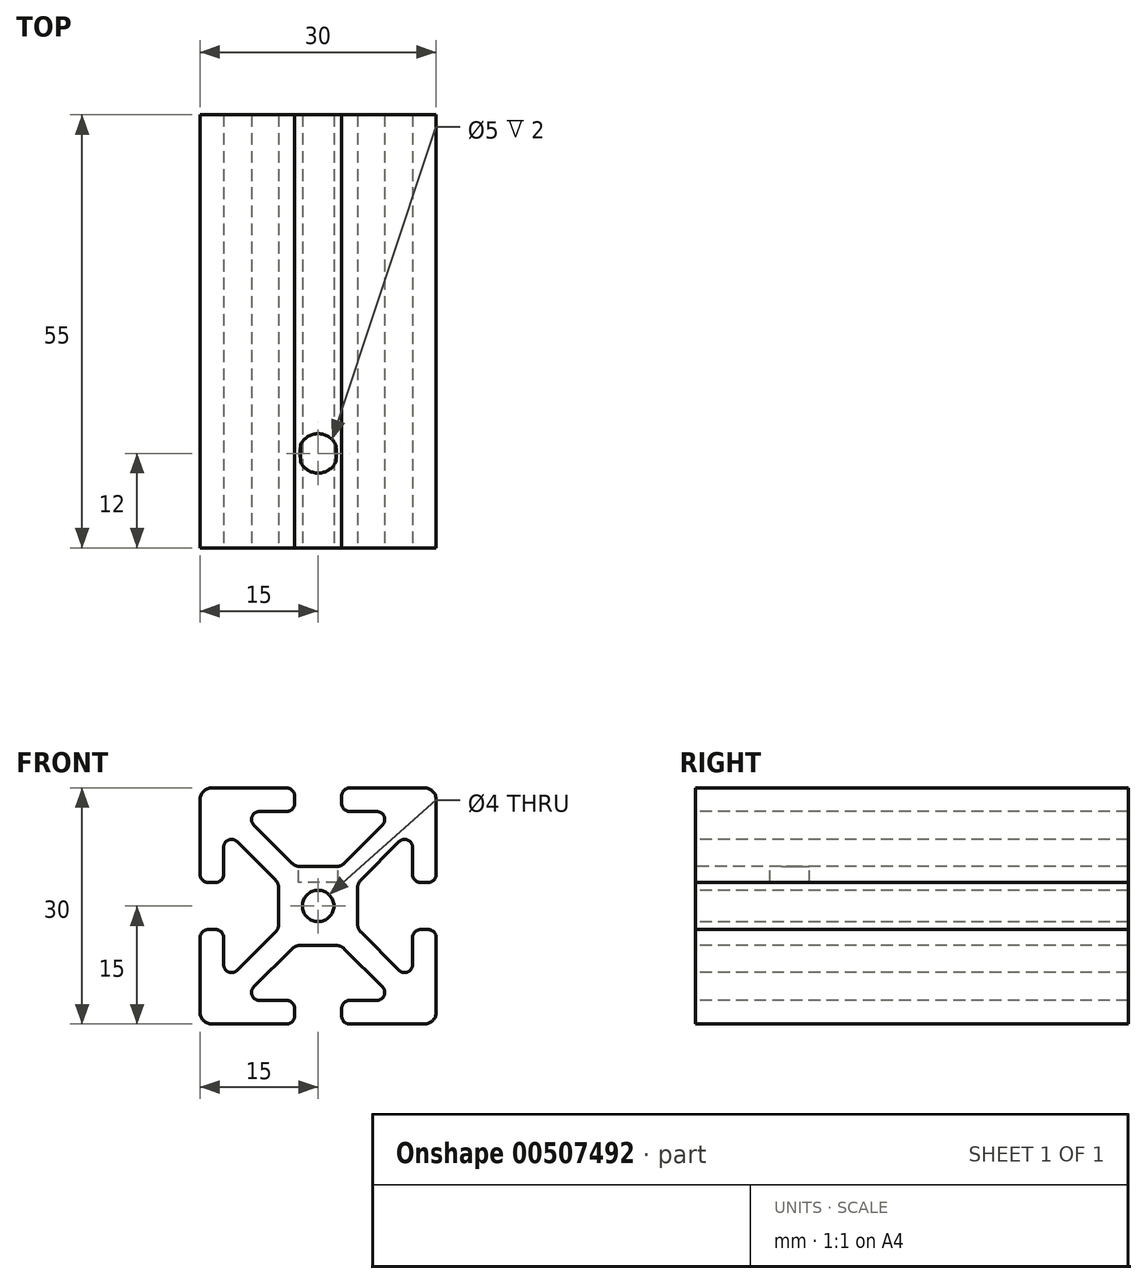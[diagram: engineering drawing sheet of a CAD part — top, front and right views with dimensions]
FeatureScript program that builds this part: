
annotation { "Feature Type Name" : "Feature", "Feature Type Description" : "" }
export const myFeature = defineFeature(function(context is Context, id is Id, definition is map)
    precondition{}
    {
        {
            var Q0;
            Q0=qCreatedBy(makeId("Front.planeOp"),FACE);
            var sketch = newSketch(context, id + "F0", { "sketchPlane" : qUnion([Q0])});
            skLineSegment(sketch, "E0.bottom", {"start": v(13.5, 15) * mm, "end": v(4, 15) * mm});
            skLineSegment(sketch, "E0.top", {"start": v(13.5, -15) * mm, "end": v(4, -15) * mm});
            skLineSegment(sketch, "E0.left", {"start": v(15, 13.5) * mm, "end": v(15, 4) * mm});
            skLineSegment(sketch, "E0.right", {"start": v(-15, 13.5) * mm, "end": v(-15, 4) * mm});
            skPoint(sketch, "E0.middle", {"position": v(0, 0) * mm});
            skLineSegment(sketch, "E1.bottom", {"start": v(7.46, 12) * mm, "end": v(4, 12) * mm});
            skLineSegment(sketch, "E1.top", {"start": v(7.46, -12) * mm, "end": v(4, -12) * mm});
            skLineSegment(sketch, "E1.left", {"start": v(12, 7.46) * mm, "end": v(12, 4) * mm});
            skLineSegment(sketch, "E1.right", {"start": v(-12, 7.46) * mm, "end": v(-12, 4) * mm});
            skLineSegment(sketch, "E2", {"start": v(8.17, 10.3) * mm, "end": v(3.32, 5.44) * mm});
            skLineSegment(sketch, "E3", {"start": v(-8.17, -10.3) * mm, "end": v(-3.32, -5.44) * mm});
            skLineSegment(sketch, "E4", {"start": v(-8.17, 10.3) * mm, "end": v(-3.32, 5.44) * mm});
            skLineSegment(sketch, "E5", {"start": v(-10.3, 8.17) * mm, "end": v(-5.44, 3.32) * mm});
            skPoint(sketch, "E6.orphan", {"position": v(12, 12) * mm});
            skPoint(sketch, "E7.orphan", {"position": v(12, -12) * mm});
            skPoint(sketch, "E8.orphan", {"position": v(-12, -12) * mm});
            skPoint(sketch, "E9.orphan", {"position": v(-12, 12) * mm});
            skLineSegment(sketch, "E10.trimOffspring", {"start": v(-5.44, -3.32) * mm, "end": v(-10.3, -8.17) * mm});
            skLineSegment(sketch, "E11.trimOffspring", {"start": v(5.44, -3.32) * mm, "end": v(10.3, -8.17) * mm});
            skLineSegment(sketch, "E12.trimOffspring", {"start": v(5.44, 3.32) * mm, "end": v(10.3, 8.17) * mm});
            skLineSegment(sketch, "E13.trimOffspring", {"start": v(3.32, -5.44) * mm, "end": v(8.17, -10.3) * mm});
            skLineSegment(sketch, "E14.bottom", {"start": v(2.26, 5) * mm, "end": v(-2.26, 5) * mm});
            skLineSegment(sketch, "E14.top", {"start": v(2.26, -5) * mm, "end": v(-2.26, -5) * mm});
            skLineSegment(sketch, "E14.left", {"start": v(5, 2.26) * mm, "end": v(5, -2.26) * mm});
            skLineSegment(sketch, "E14.right", {"start": v(-5, 2.26) * mm, "end": v(-5, -2.26) * mm});
            skPoint(sketch, "E15.orphan", {"position": v(5, 5) * mm});
            skPoint(sketch, "E16.orphan", {"position": v(5, -5) * mm});
            skPoint(sketch, "E17.orphan", {"position": v(-5, -5) * mm});
            skPoint(sketch, "E18.orphan", {"position": v(-5, 5) * mm});
            skCircle(sketch, "E19", {"center": v(0, 0) * mm, "radius": 2 * mm});
            skLineSegment(sketch, "E20", {"start": v(-3, 14) * mm, "end": v(-3, 13) * mm});
            skLineSegment(sketch, "E21", {"start": v(3, 14) * mm, "end": v(3, 13) * mm});
            skLineSegment(sketch, "E22.trimOffspring", {"start": v(-3, -13) * mm, "end": v(-3, -14) * mm});
            skLineSegment(sketch, "E23.trimOffspring", {"start": v(-4, 12) * mm, "end": v(-7.46, 12) * mm});
            skLineSegment(sketch, "E24.trimOffspring", {"start": v(-4, 15) * mm, "end": v(-13.5, 15) * mm});
            skLineSegment(sketch, "E25.trimOffspring", {"start": v(3, -13) * mm, "end": v(3, -14) * mm});
            skLineSegment(sketch, "E26.trimOffspring", {"start": v(-4, -12) * mm, "end": v(-7.46, -12) * mm});
            skLineSegment(sketch, "E27.trimOffspring", {"start": v(-4, -15) * mm, "end": v(-13.5, -15) * mm});
            skLineSegment(sketch, "E28", {"start": v(-14, 3) * mm, "end": v(-13, 3) * mm});
            skLineSegment(sketch, "E29", {"start": v(-14, -3) * mm, "end": v(-13, -3) * mm});
            skLineSegment(sketch, "E30.trimOffspring", {"start": v(-12, -4) * mm, "end": v(-12, -7.46) * mm});
            skLineSegment(sketch, "E31.trimOffspring", {"start": v(-15, -4) * mm, "end": v(-15, -13.5) * mm});
            skLineSegment(sketch, "E32.trimOffspring", {"start": v(13, 3) * mm, "end": v(14, 3) * mm});
            skLineSegment(sketch, "E33.trimOffspring", {"start": v(13, -3) * mm, "end": v(14, -3) * mm});
            skLineSegment(sketch, "E34.trimOffspring", {"start": v(12, -4) * mm, "end": v(12, -7.46) * mm});
            skLineSegment(sketch, "E35.trimOffspring", {"start": v(15, -4) * mm, "end": v(15, -13.5) * mm});
            skPoint(sketch, "E36.visualSharp", {"position": v(-15, 15) * mm});
            skArc(sketch, "E36.filletArc", {"start": v(-13.5, 15) * mm, "mid": v(-14.56, 14.56) * mm, "end": v(-15, 13.5) * mm});
            skPoint(sketch, "E37.visualSharp", {"position": v(15, 15) * mm});
            skArc(sketch, "E37.filletArc", {"start": v(15, 13.5) * mm, "mid": v(14.56, 14.56) * mm, "end": v(13.5, 15) * mm});
            skPoint(sketch, "E38.visualSharp", {"position": v(15, -15) * mm});
            skArc(sketch, "E38.filletArc", {"start": v(13.5, -15) * mm, "mid": v(14.56, -14.56) * mm, "end": v(15, -13.5) * mm});
            skPoint(sketch, "E39.visualSharp", {"position": v(-15, -15) * mm});
            skArc(sketch, "E39.filletArc", {"start": v(-15, -13.5) * mm, "mid": v(-14.56, -14.56) * mm, "end": v(-13.5, -15) * mm});
            skPoint(sketch, "E40.visualSharp", {"position": v(-5, -2.88) * mm});
            skArc(sketch, "E40.filletArc", {"start": v(-5.44, -3.32) * mm, "mid": v(-5.11, -2.83) * mm, "end": v(-5, -2.26) * mm});
            skPoint(sketch, "E41.visualSharp", {"position": v(-2.88, -5) * mm});
            skArc(sketch, "E41.filletArc", {"start": v(-2.26, -5) * mm, "mid": v(-2.83, -5.11) * mm, "end": v(-3.32, -5.44) * mm});
            skPoint(sketch, "E42.visualSharp", {"position": v(2.88, -5) * mm});
            skArc(sketch, "E42.filletArc", {"start": v(3.32, -5.44) * mm, "mid": v(2.83, -5.11) * mm, "end": v(2.26, -5) * mm});
            skPoint(sketch, "E43.visualSharp", {"position": v(5, -2.88) * mm});
            skArc(sketch, "E43.filletArc", {"start": v(5, -2.26) * mm, "mid": v(5.11, -2.83) * mm, "end": v(5.44, -3.32) * mm});
            skPoint(sketch, "E44.visualSharp", {"position": v(5, 2.88) * mm});
            skArc(sketch, "E44.filletArc", {"start": v(5.44, 3.32) * mm, "mid": v(5.11, 2.83) * mm, "end": v(5, 2.26) * mm});
            skPoint(sketch, "E45.visualSharp", {"position": v(2.88, 5) * mm});
            skArc(sketch, "E45.filletArc", {"start": v(2.26, 5) * mm, "mid": v(2.83, 5.11) * mm, "end": v(3.32, 5.44) * mm});
            skPoint(sketch, "E46.visualSharp", {"position": v(-2.88, 5) * mm});
            skArc(sketch, "E46.filletArc", {"start": v(-3.32, 5.44) * mm, "mid": v(-2.83, 5.11) * mm, "end": v(-2.26, 5) * mm});
            skPoint(sketch, "E47.visualSharp", {"position": v(-3, 12) * mm});
            skArc(sketch, "E47.filletArc", {"start": v(-4, 12) * mm, "mid": v(-3.3, 12.3) * mm, "end": v(-3, 13) * mm});
            skPoint(sketch, "E48.visualSharp", {"position": v(-3, 15) * mm});
            skArc(sketch, "E48.filletArc", {"start": v(-3, 14) * mm, "mid": v(-3.3, 14.7) * mm, "end": v(-4, 15) * mm});
            skPoint(sketch, "E49.visualSharp", {"position": v(3, 15) * mm});
            skArc(sketch, "E49.filletArc", {"start": v(4, 15) * mm, "mid": v(3.3, 14.7) * mm, "end": v(3, 14) * mm});
            skPoint(sketch, "E50.visualSharp", {"position": v(3, 12) * mm});
            skArc(sketch, "E50.filletArc", {"start": v(3, 13) * mm, "mid": v(3.3, 12.3) * mm, "end": v(4, 12) * mm});
            skPoint(sketch, "E51.visualSharp", {"position": v(12, 3) * mm});
            skArc(sketch, "E51.filletArc", {"start": v(12, 4) * mm, "mid": v(12.3, 3.3) * mm, "end": v(13, 3) * mm});
            skPoint(sketch, "E52.visualSharp", {"position": v(15, 3) * mm});
            skArc(sketch, "E52.filletArc", {"start": v(14, 3) * mm, "mid": v(14.7, 3.3) * mm, "end": v(15, 4) * mm});
            skPoint(sketch, "E53.visualSharp", {"position": v(15, -3) * mm});
            skArc(sketch, "E53.filletArc", {"start": v(15, -4) * mm, "mid": v(14.7, -3.3) * mm, "end": v(14, -3) * mm});
            skPoint(sketch, "E54.visualSharp", {"position": v(12, -3) * mm});
            skArc(sketch, "E54.filletArc", {"start": v(13, -3) * mm, "mid": v(12.3, -3.3) * mm, "end": v(12, -4) * mm});
            skPoint(sketch, "E55.visualSharp", {"position": v(3, -12) * mm});
            skArc(sketch, "E55.filletArc", {"start": v(4, -12) * mm, "mid": v(3.3, -12.3) * mm, "end": v(3, -13) * mm});
            skPoint(sketch, "E56.visualSharp", {"position": v(3, -15) * mm});
            skArc(sketch, "E56.filletArc", {"start": v(3, -14) * mm, "mid": v(3.3, -14.7) * mm, "end": v(4, -15) * mm});
            skPoint(sketch, "E57.visualSharp", {"position": v(-3, -12) * mm});
            skArc(sketch, "E57.filletArc", {"start": v(-3, -13) * mm, "mid": v(-3.3, -12.3) * mm, "end": v(-4, -12) * mm});
            skPoint(sketch, "E58.visualSharp", {"position": v(-3, -15) * mm});
            skArc(sketch, "E58.filletArc", {"start": v(-4, -15) * mm, "mid": v(-3.3, -14.7) * mm, "end": v(-3, -14) * mm});
            skPoint(sketch, "E59.visualSharp", {"position": v(-12, -3) * mm});
            skArc(sketch, "E59.filletArc", {"start": v(-12, -4) * mm, "mid": v(-12.3, -3.3) * mm, "end": v(-13, -3) * mm});
            skPoint(sketch, "E60.visualSharp", {"position": v(-15, -3) * mm});
            skArc(sketch, "E60.filletArc", {"start": v(-14, -3) * mm, "mid": v(-14.7, -3.3) * mm, "end": v(-15, -4) * mm});
            skPoint(sketch, "E61.visualSharp", {"position": v(-15, 3) * mm});
            skArc(sketch, "E61.filletArc", {"start": v(-15, 4) * mm, "mid": v(-14.7, 3.3) * mm, "end": v(-14, 3) * mm});
            skPoint(sketch, "E62.visualSharp", {"position": v(-12, 3) * mm});
            skArc(sketch, "E62.filletArc", {"start": v(-13, 3) * mm, "mid": v(-12.3, 3.3) * mm, "end": v(-12, 4) * mm});
            skPoint(sketch, "E63.visualSharp", {"position": v(9.88, 12) * mm});
            skArc(sketch, "E63.filletArc", {"start": v(8.17, 10.3) * mm, "mid": v(8.39, 11.38) * mm, "end": v(7.46, 12) * mm});
            skPoint(sketch, "E64.visualSharp", {"position": v(12, 9.88) * mm});
            skArc(sketch, "E64.filletArc", {"start": v(12, 7.46) * mm, "mid": v(11.38, 8.39) * mm, "end": v(10.3, 8.17) * mm});
            skPoint(sketch, "E65.visualSharp", {"position": v(12, -9.88) * mm});
            skArc(sketch, "E65.filletArc", {"start": v(10.3, -8.17) * mm, "mid": v(11.38, -8.39) * mm, "end": v(12, -7.46) * mm});
            skPoint(sketch, "E66.visualSharp", {"position": v(9.88, -12) * mm});
            skArc(sketch, "E66.filletArc", {"start": v(7.46, -12) * mm, "mid": v(8.39, -11.38) * mm, "end": v(8.17, -10.3) * mm});
            skPoint(sketch, "E67.visualSharp", {"position": v(-12, -9.88) * mm});
            skArc(sketch, "E67.filletArc", {"start": v(-12, -7.46) * mm, "mid": v(-11.38, -8.39) * mm, "end": v(-10.3, -8.17) * mm});
            skPoint(sketch, "E68.visualSharp", {"position": v(-9.88, -12) * mm});
            skArc(sketch, "E68.filletArc", {"start": v(-8.17, -10.3) * mm, "mid": v(-8.39, -11.38) * mm, "end": v(-7.46, -12) * mm});
            skPoint(sketch, "E69.visualSharp", {"position": v(-12, 9.88) * mm});
            skArc(sketch, "E69.filletArc", {"start": v(-10.3, 8.17) * mm, "mid": v(-11.38, 8.39) * mm, "end": v(-12, 7.46) * mm});
            skPoint(sketch, "E70.visualSharp", {"position": v(-9.88, 12) * mm});
            skArc(sketch, "E70.filletArc", {"start": v(-7.46, 12) * mm, "mid": v(-8.39, 11.38) * mm, "end": v(-8.17, 10.3) * mm});
            skPoint(sketch, "E71.visualSharp", {"position": v(-5, 2.88) * mm});
            skArc(sketch, "E71.filletArc", {"start": v(-5, 2.26) * mm, "mid": v(-5.11, 2.83) * mm, "end": v(-5.44, 3.32) * mm});
            skSolve(sketch);
        }
        {
            var Q0;
            Q0=qSketchRegion(id+"F0",true);
            extrude(context, id + "F1", {"entities" : qUnion([Q0]), "oppositeDirection" : true, "depth" : 55 * mm});
        }
        {
            var Q0;
            Q0=makeQuery(id+"F1.opExtrude","SWEPT_FACE",FACE,{"disambiguationData":[OSD([sQuery(id+"F0.wireOp",EDGE,"E14.bottom")])]});
            var sketch = newSketch(context, id + "F2", { "sketchPlane" : qUnion([Q0])});
            skCircle(sketch, "E72", {"center": v(0, 12) * mm, "radius": 2.5 * mm});
            skSolve(sketch);
        }
        {
            var Q0;
            Q0 = qSketchRegion(id + "F2", true);
            extrude(context, id + "F3", {"entities" : qUnion([Q0]), "operationType" : NewBodyOperationType.REMOVE, "oppositeDirection" : true, "depth" : 2 * mm});
        }
    });
